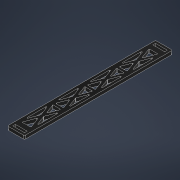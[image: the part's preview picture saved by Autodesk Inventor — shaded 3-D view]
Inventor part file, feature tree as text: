
AUTODESK INVENTOR PART (.ipt)
format: ipt  version: 2021 (Build 250183000, 183)  size: 266,752 bytes
history: native  units: mm
features: extrude x1, fillet x1, sketch x1
ambient origin geometry x8: Origin, YZ Plane, XZ Plane, XY Plane, X Axis, Y Axis, Z Axis, Center Point
bodies: Body1 (feature_tree)
feature tree (3):
  extrude  "Extrusion2"  Depth=2.0mm
  fillet  "Fillet1"  Radius=1.0mm
  sketch  "Sketch1"  dims[d6=13.6mm d10=2.0mm d11=1.0mm d12=2.0mm d15=9.6mm d16=52.5mm d17=4.0mm d21=2.0mm d22=2.0mm d23=2.0mm d25=2.0mm d26=2.0mm d28=2.0mm d29=2.0mm d30=2.0mm d31=2.0mm d32=2.0mm d33=2.0mm d38=2.0mm d39=2.0mm d40=2.0mm d41=2.0mm d42=2.0mm d43=2.0mm d44=2.6mm d45=0.0mm d46=0.4mm]
